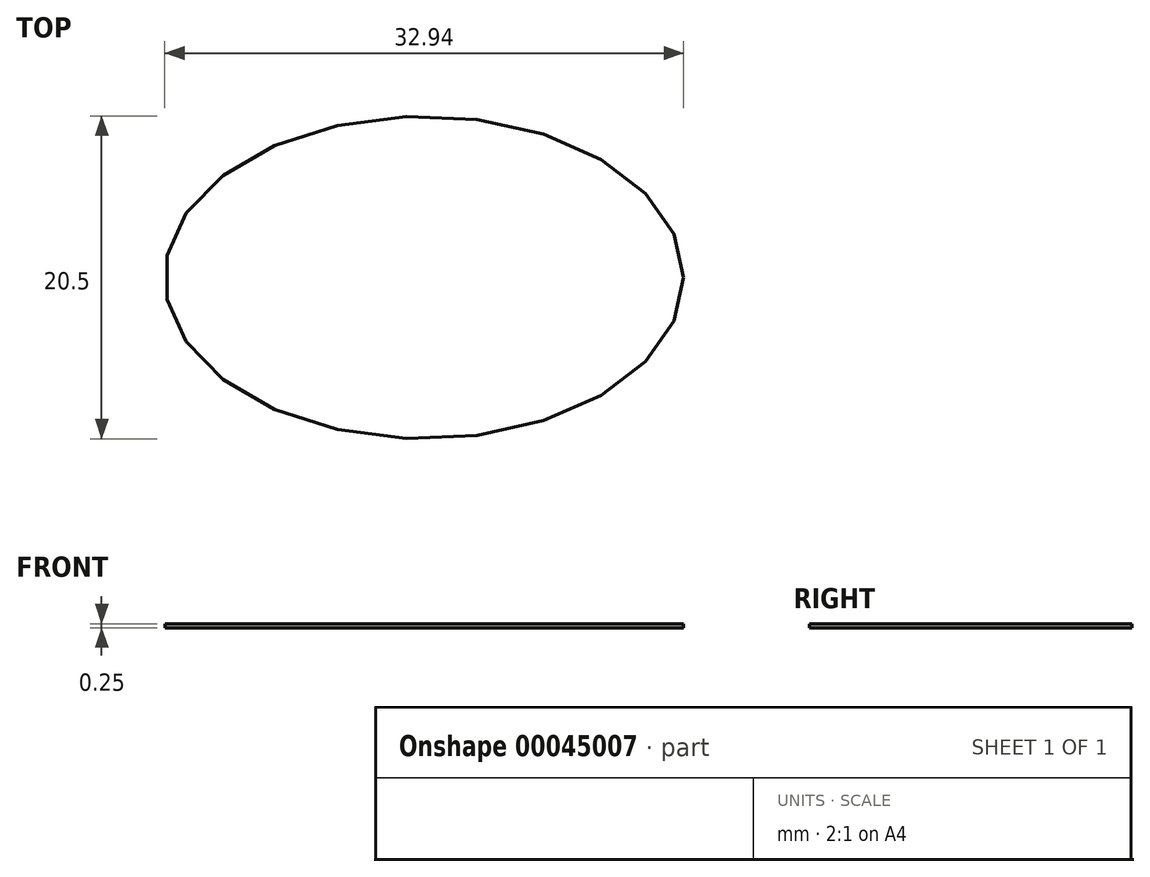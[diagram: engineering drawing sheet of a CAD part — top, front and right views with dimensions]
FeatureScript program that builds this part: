
annotation { "Feature Type Name" : "Feature", "Feature Type Description" : "" }
export const myFeature = defineFeature(function(context is Context, id is Id, definition is map)
    precondition{}
    {
        {
            var Q0;
            Q0=qCreatedBy(makeId("Top.planeOp"),FACE);
            var sketch = newSketch(context, id + "F0", { "sketchPlane" : qUnion([Q0])});
            skEllipse(sketch, "E0", {"center": v(-56.22, 51.25) * mm, "majorRadius": 16.47 * mm, "minorRadius": 10.25 * mm, "majorAxis": v(1, 0)});
            skEllipse(sketch, "E1", {"center": v(30.38, 51.25) * mm, "majorRadius": 15.9 * mm, "minorRadius": 10.82 * mm, "majorAxis": v(1, 0)});
            skSolve(sketch);
        }
        {
            var Q0;
            Q0=makeQuery(id+"F0.imprint","IMPRINT",FACE,{"disambiguationData":[TD([[makeQuery(id+"F0.imprint","IMPRINT",EDGE,{"derivedFrom":sQuery(id+"F0.wireOp",EDGE,"E0")}),1.0]])]});
            extrude(context, id + "F1", {"entities" : qUnion([Q0]), "depth" : 0.25 * mm});
        }
    });
